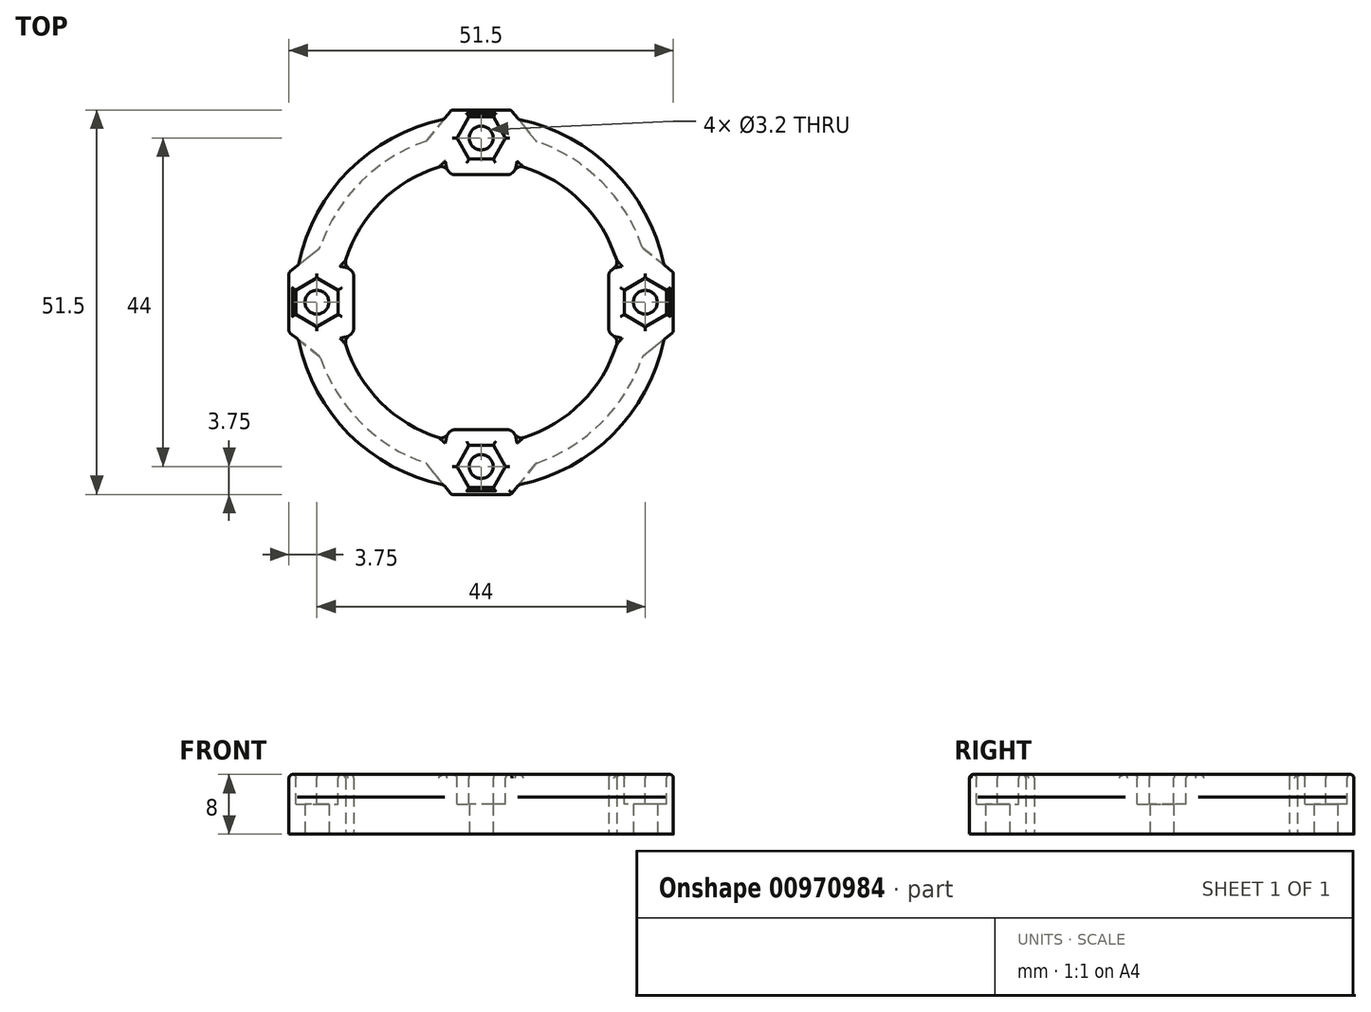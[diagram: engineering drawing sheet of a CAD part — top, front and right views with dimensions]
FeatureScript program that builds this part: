
annotation { "Feature Type Name" : "Feature", "Feature Type Description" : "" }
export const myFeature = defineFeature(function(context is Context, id is Id, definition is map)
    precondition{}
    {
        {
            var Q0;
            Q0=qCreatedBy(makeId("Top.planeOp"),FACE);
            var sketch = newSketch(context, id + "F0", { "sketchPlane" : qUnion([Q0])});
            skArc(sketch, "E0", {"start": v(-5, 24.5) * mm, "mid": v(-17.68, 17.68) * mm, "end": v(-24.5, 5) * mm});
            skLineSegment(sketch, "E1.bottom", {"start": v(-4, 25.75) * mm, "end": v(4, 25.75) * mm});
            skLineSegment(sketch, "E1.top", {"start": v(-4, -25.75) * mm, "end": v(4, -25.75) * mm});
            skLineSegment(sketch, "E1.left", {"start": v(-25.75, 4) * mm, "end": v(-25.75, -4) * mm});
            skLineSegment(sketch, "E1.right", {"start": v(25.75, 4) * mm, "end": v(25.75, -4) * mm});
            skLineSegment(sketch, "E2", {"start": v(-5, 24.5) * mm, "end": v(-4, 25.75) * mm});
            skLineSegment(sketch, "E3", {"start": v(4, 25.75) * mm, "end": v(5, 24.5) * mm});
            skLineSegment(sketch, "E4.1.0", {"start": v(-24.5, -5) * mm, "end": v(-25.75, -4) * mm});
            skLineSegment(sketch, "E4.1.1", {"start": v(-25.75, 4) * mm, "end": v(-24.5, 5) * mm});
            skLineSegment(sketch, "E4.2.0", {"start": v(5, -24.5) * mm, "end": v(4, -25.75) * mm});
            skLineSegment(sketch, "E4.2.1", {"start": v(-4, -25.75) * mm, "end": v(-5, -24.5) * mm});
            skLineSegment(sketch, "E4.3.0", {"start": v(24.5, 5) * mm, "end": v(25.75, 4) * mm});
            skLineSegment(sketch, "E4.3.1", {"start": v(25.75, -4) * mm, "end": v(24.5, -5) * mm});
            skPoint(sketch, "E5.orphan", {"position": v(-25.75, 25.75) * mm});
            skPoint(sketch, "E6.orphan", {"position": v(25.75, 25.75) * mm});
            skArc(sketch, "E7.trimOffspring", {"start": v(24.5, 5) * mm, "mid": v(17.68, 17.68) * mm, "end": v(5, 24.5) * mm});
            skPoint(sketch, "E8.orphan", {"position": v(25.75, -25.75) * mm});
            skArc(sketch, "E9.trimOffspring", {"start": v(5, -24.5) * mm, "mid": v(17.68, -17.68) * mm, "end": v(24.5, -5) * mm});
            skPoint(sketch, "E10.orphan", {"position": v(-25.75, -25.75) * mm});
            skArc(sketch, "E11.trimOffspring", {"start": v(-24.5, -5) * mm, "mid": v(-17.68, -17.68) * mm, "end": v(-5, -24.5) * mm});
            skCircle(sketch, "E12", {"center": v(0, 22) * mm, "radius": 1.6 * mm});
            skCircle(sketch, "E13", {"center": v(-22, 0) * mm, "radius": 1.6 * mm});
            skCircle(sketch, "E14", {"center": v(22, 0) * mm, "radius": 1.6 * mm});
            skCircle(sketch, "E15", {"center": v(0, -22) * mm, "radius": 1.6 * mm});
            skCircle(sketch, "E16", {"center": v(0, 0) * mm, "radius": 22 * mm, "construction": true});
            skArc(sketch, "E17", {"start": v(-5, 18.33) * mm, "mid": v(-13.44, 13.44) * mm, "end": v(-18.33, 5) * mm});
            skLineSegment(sketch, "E18", {"start": v(-5, 18.33) * mm, "end": v(-4, 17.08) * mm});
            skLineSegment(sketch, "E19", {"start": v(-4, 17.08) * mm, "end": v(4, 17.08) * mm});
            skLineSegment(sketch, "E20", {"start": v(4, 17.08) * mm, "end": v(5, 18.33) * mm});
            skLineSegment(sketch, "E21.1.0", {"start": v(-18.33, -5) * mm, "end": v(-17.08, -4) * mm});
            skLineSegment(sketch, "E21.1.1", {"start": v(-17.08, -4) * mm, "end": v(-17.08, 4) * mm});
            skLineSegment(sketch, "E21.1.2", {"start": v(-17.08, 4) * mm, "end": v(-18.33, 5) * mm});
            skLineSegment(sketch, "E21.2.0", {"start": v(5, -18.33) * mm, "end": v(4, -17.08) * mm});
            skLineSegment(sketch, "E21.2.1", {"start": v(4, -17.08) * mm, "end": v(-4, -17.08) * mm});
            skLineSegment(sketch, "E21.2.2", {"start": v(-4, -17.08) * mm, "end": v(-5, -18.33) * mm});
            skLineSegment(sketch, "E21.3.0", {"start": v(18.33, 5) * mm, "end": v(17.08, 4) * mm});
            skLineSegment(sketch, "E21.3.1", {"start": v(17.08, 4) * mm, "end": v(17.08, -4) * mm});
            skLineSegment(sketch, "E21.3.2", {"start": v(17.08, -4) * mm, "end": v(18.33, -5) * mm});
            skArc(sketch, "E22.trimOffspring", {"start": v(18.33, 5) * mm, "mid": v(13.44, 13.44) * mm, "end": v(5, 18.33) * mm});
            skArc(sketch, "E23.trimOffspring", {"start": v(5, -18.33) * mm, "mid": v(13.44, -13.44) * mm, "end": v(18.33, -5) * mm});
            skArc(sketch, "E24.trimOffspring", {"start": v(-18.33, -5) * mm, "mid": v(-13.44, -13.44) * mm, "end": v(-5, -18.33) * mm});
            skSolve(sketch);
        }
        {
            assignVariable(context, id + "F1", {"name" : "nuth", "anyValue" : 4});
        }
        {
            assignVariable(context, id + "F2", {"name" : "bodyt", "anyValue" : 4});
        }
        {
            var Q0;
            Q0=makeQuery(id+"F0.imprint","IMPRINT",FACE,{"disambiguationData":[TD([[makeQuery(id+"F0.imprint","IMPRINT",EDGE,{"derivedFrom":sQuery(id+"F0.wireOp",EDGE,"E0")}),1.0]])]});
            extrude(context, id + "F3", {"entities" : qUnion([Q0]), "depth" : (getVariable(context, 'nuth') + getVariable(context, 'bodyt')) * mm, "offsetDistance" : 25 * mm});
        }
        {
            var Q0;
            Q0=makeQuery(id+"F3.opExtrude","CAP_FACE",FACE,{"disambiguationData":[OSD([sQuery(id+"F0.wireOp",EDGE,"E0"),sQuery(id+"F0.wireOp",EDGE,"E1.bottom"),sQuery(id+"F0.wireOp",EDGE,"E1.top"),sQuery(id+"F0.wireOp",EDGE,"E1.left"),sQuery(id+"F0.wireOp",EDGE,"E1.right"),sQuery(id+"F0.wireOp",EDGE,"E2"),sQuery(id+"F0.wireOp",EDGE,"E3"),sQuery(id+"F0.wireOp",EDGE,"E4.1.0"),sQuery(id+"F0.wireOp",EDGE,"E4.1.1"),sQuery(id+"F0.wireOp",EDGE,"E4.2.0"),sQuery(id+"F0.wireOp",EDGE,"E4.2.1"),sQuery(id+"F0.wireOp",EDGE,"E4.3.0"),sQuery(id+"F0.wireOp",EDGE,"E4.3.1"),sQuery(id+"F0.wireOp",EDGE,"E7.trimOffspring"),sQuery(id+"F0.wireOp",EDGE,"E9.trimOffspring"),sQuery(id+"F0.wireOp",EDGE,"E11.trimOffspring"),sQuery(id+"F0.wireOp",EDGE,"E12"),sQuery(id+"F0.wireOp",EDGE,"E13"),sQuery(id+"F0.wireOp",EDGE,"E14"),sQuery(id+"F0.wireOp",EDGE,"E15")])],"isStart":false});
            var sketch = newSketch(context, id + "F4", { "sketchPlane" : qUnion([Q0])});
            skCircle(sketch, "E25.0", {"center": v(0, 22) * mm, "radius": 1.6 * mm, "construction": true});
            skCircle(sketch, "E26.cCircle", {"center": v(0, 22) * mm, "radius": 2.83 * mm, "construction": true});
            skLineSegment(sketch, "E26.0", {"start": v(1.63, 24.82) * mm, "end": v(3.26, 22) * mm});
            skLineSegment(sketch, "E26.1", {"start": v(3.26, 22) * mm, "end": v(1.63, 19.17) * mm});
            skLineSegment(sketch, "E26.2", {"start": v(1.63, 19.17) * mm, "end": v(-1.63, 19.17) * mm});
            skLineSegment(sketch, "E26.3", {"start": v(-1.63, 19.17) * mm, "end": v(-3.26, 22) * mm});
            skLineSegment(sketch, "E26.4", {"start": v(-3.26, 22) * mm, "end": v(-1.63, 24.82) * mm});
            skLineSegment(sketch, "E26.5", {"start": v(-1.63, 24.82) * mm, "end": v(1.63, 24.82) * mm});
            skPoint(sketch, "E26.0.midPoint", {"position": v(2.45, 23.41) * mm});
            skCircle(sketch, "E27.1.0", {"center": v(-22, 0) * mm, "radius": 1.6 * mm, "construction": true});
            skCircle(sketch, "E27.1.1", {"center": v(-22, 0) * mm, "radius": 2.83 * mm, "construction": true});
            skLineSegment(sketch, "E27.1.2", {"start": v(-19.17, -1.63) * mm, "end": v(-22, -3.26) * mm});
            skPoint(sketch, "E27.1.3", {"position": v(-23.41, 2.45) * mm});
            skLineSegment(sketch, "E27.1.4", {"start": v(-22, -3.26) * mm, "end": v(-24.82, -1.63) * mm});
            skLineSegment(sketch, "E27.1.5", {"start": v(-24.82, 1.63) * mm, "end": v(-22, 3.26) * mm});
            skLineSegment(sketch, "E27.1.6", {"start": v(-22, 3.26) * mm, "end": v(-19.17, 1.63) * mm});
            skLineSegment(sketch, "E27.1.7", {"start": v(-19.17, 1.63) * mm, "end": v(-19.17, -1.63) * mm});
            skLineSegment(sketch, "E27.1.8", {"start": v(-24.82, -1.63) * mm, "end": v(-24.82, 1.63) * mm});
            skCircle(sketch, "E27.2.0", {"center": v(0, -22) * mm, "radius": 1.6 * mm, "construction": true});
            skCircle(sketch, "E27.2.1", {"center": v(0, -22) * mm, "radius": 2.83 * mm, "construction": true});
            skLineSegment(sketch, "E27.2.2", {"start": v(1.63, -19.17) * mm, "end": v(3.26, -22) * mm});
            skPoint(sketch, "E27.2.3", {"position": v(-2.45, -23.41) * mm});
            skLineSegment(sketch, "E27.2.4", {"start": v(3.26, -22) * mm, "end": v(1.63, -24.82) * mm});
            skLineSegment(sketch, "E27.2.5", {"start": v(-1.63, -24.82) * mm, "end": v(-3.26, -22) * mm});
            skLineSegment(sketch, "E27.2.6", {"start": v(-3.26, -22) * mm, "end": v(-1.63, -19.17) * mm});
            skLineSegment(sketch, "E27.2.7", {"start": v(-1.63, -19.17) * mm, "end": v(1.63, -19.17) * mm});
            skLineSegment(sketch, "E27.2.8", {"start": v(1.63, -24.82) * mm, "end": v(-1.63, -24.82) * mm});
            skCircle(sketch, "E27.3.0", {"center": v(22, 0) * mm, "radius": 1.6 * mm, "construction": true});
            skCircle(sketch, "E27.3.1", {"center": v(22, 0) * mm, "radius": 2.83 * mm, "construction": true});
            skLineSegment(sketch, "E27.3.2", {"start": v(19.17, 1.63) * mm, "end": v(22, 3.26) * mm});
            skPoint(sketch, "E27.3.3", {"position": v(23.41, -2.45) * mm});
            skLineSegment(sketch, "E27.3.4", {"start": v(22, 3.26) * mm, "end": v(24.82, 1.63) * mm});
            skLineSegment(sketch, "E27.3.5", {"start": v(24.82, -1.63) * mm, "end": v(22, -3.26) * mm});
            skLineSegment(sketch, "E27.3.6", {"start": v(22, -3.26) * mm, "end": v(19.17, -1.63) * mm});
            skLineSegment(sketch, "E27.3.7", {"start": v(19.17, -1.63) * mm, "end": v(19.17, 1.63) * mm});
            skLineSegment(sketch, "E27.3.8", {"start": v(24.82, 1.63) * mm, "end": v(24.82, -1.63) * mm});
            skPoint(sketch, "E27.center", {"position": v(0, 0) * mm});
            skSolve(sketch);
        }
        {
            var Q0;
            Q0 = qSketchRegion(id + "F4", true);
            extrude(context, id + "F5", {"entities" : qUnion([Q0]), "operationType" : NewBodyOperationType.REMOVE, "oppositeDirection" : true, "depth" : (getVariable(context, 'nuth')) * mm, "offsetDistance" : 25 * mm});
        }
        {
            var Q0;
            Q0=makeQuery(id+"F3.opExtrude","CAP_FACE",FACE,{"disambiguationData":[OSD([sQuery(id+"F0.wireOp",EDGE,"E0"),sQuery(id+"F0.wireOp",EDGE,"E1.bottom"),sQuery(id+"F0.wireOp",EDGE,"E1.top"),sQuery(id+"F0.wireOp",EDGE,"E1.left"),sQuery(id+"F0.wireOp",EDGE,"E1.right"),sQuery(id+"F0.wireOp",EDGE,"E2"),sQuery(id+"F0.wireOp",EDGE,"E3"),sQuery(id+"F0.wireOp",EDGE,"E4.1.0"),sQuery(id+"F0.wireOp",EDGE,"E4.1.1"),sQuery(id+"F0.wireOp",EDGE,"E4.2.0"),sQuery(id+"F0.wireOp",EDGE,"E4.2.1"),sQuery(id+"F0.wireOp",EDGE,"E4.3.0"),sQuery(id+"F0.wireOp",EDGE,"E4.3.1"),sQuery(id+"F0.wireOp",EDGE,"E7.trimOffspring"),sQuery(id+"F0.wireOp",EDGE,"E9.trimOffspring"),sQuery(id+"F0.wireOp",EDGE,"E11.trimOffspring"),sQuery(id+"F0.wireOp",EDGE,"E12"),sQuery(id+"F0.wireOp",EDGE,"E13"),sQuery(id+"F0.wireOp",EDGE,"E14"),sQuery(id+"F0.wireOp",EDGE,"E15"),sQuery(id+"F0.wireOp",EDGE,"E17"),sQuery(id+"F0.wireOp",EDGE,"E18"),sQuery(id+"F0.wireOp",EDGE,"E19"),sQuery(id+"F0.wireOp",EDGE,"E20"),sQuery(id+"F0.wireOp",EDGE,"E21.1.0"),sQuery(id+"F0.wireOp",EDGE,"E21.1.1"),sQuery(id+"F0.wireOp",EDGE,"E21.1.2"),sQuery(id+"F0.wireOp",EDGE,"E21.2.0"),sQuery(id+"F0.wireOp",EDGE,"E21.2.1"),sQuery(id+"F0.wireOp",EDGE,"E21.2.2"),sQuery(id+"F0.wireOp",EDGE,"E21.3.0"),sQuery(id+"F0.wireOp",EDGE,"E21.3.1"),sQuery(id+"F0.wireOp",EDGE,"E21.3.2"),sQuery(id+"F0.wireOp",EDGE,"E22.trimOffspring"),sQuery(id+"F0.wireOp",EDGE,"E23.trimOffspring"),sQuery(id+"F0.wireOp",EDGE,"E24.trimOffspring")])],"isStart":true});
            var sketch = newSketch(context, id + "F6", { "sketchPlane" : qUnion([Q0])});
            skArc(sketch, "E28.0", {"start": v(-24.5, 5) * mm, "mid": v(-17.68, 17.68) * mm, "end": v(-5, 24.5) * mm});
            skArc(sketch, "E29.0", {"start": v(-5, -24.5) * mm, "mid": v(-17.68, -17.68) * mm, "end": v(-24.5, -5) * mm});
            skArc(sketch, "E30.0", {"start": v(5, 24.5) * mm, "mid": v(17.68, 17.68) * mm, "end": v(24.5, 5) * mm});
            skArc(sketch, "E31.0", {"start": v(24.5, -5) * mm, "mid": v(17.68, -17.68) * mm, "end": v(5, -24.5) * mm});
            skPoint(sketch, "E32.0", {"position": v(25.75, 4) * mm});
            skPoint(sketch, "E33.0", {"position": v(25.75, -4) * mm});
            skPoint(sketch, "E34.0", {"position": v(4, 25.75) * mm});
            skPoint(sketch, "E35.0", {"position": v(-4, 25.75) * mm});
            skPoint(sketch, "E36.0", {"position": v(-25.75, 4) * mm});
            skPoint(sketch, "E37.0", {"position": v(-25.75, -4) * mm});
            skPoint(sketch, "E38.0", {"position": v(-4, -25.75) * mm});
            skPoint(sketch, "E39.0", {"position": v(4, -25.75) * mm});
            skLineSegment(sketch, "E40", {"start": v(-25.75, 4) * mm, "end": v(-21.6, 7.3) * mm});
            skLineSegment(sketch, "E41", {"start": v(-25.75, -4) * mm, "end": v(-21.6, -7.3) * mm});
            skLineSegment(sketch, "E42", {"start": v(-4, -25.75) * mm, "end": v(-7.3, -21.6) * mm});
            skLineSegment(sketch, "E43", {"start": v(4, -25.75) * mm, "end": v(7.3, -21.6) * mm});
            skLineSegment(sketch, "E44", {"start": v(25.75, 4) * mm, "end": v(21.6, 7.3) * mm});
            skLineSegment(sketch, "E45", {"start": v(25.75, -4) * mm, "end": v(21.6, -7.3) * mm});
            skLineSegment(sketch, "E46", {"start": v(4, 25.75) * mm, "end": v(7.3, 21.6) * mm});
            skLineSegment(sketch, "E47", {"start": v(-4, 25.75) * mm, "end": v(-7.3, 21.6) * mm});
            skArc(sketch, "E48", {"start": v(-21.6, -7.3) * mm, "mid": v(-16.12, -16.12) * mm, "end": v(-7.3, -21.6) * mm});
            skArc(sketch, "E49.trimOffspring", {"start": v(-7.3, 21.6) * mm, "mid": v(-16.12, 16.12) * mm, "end": v(-21.6, 7.3) * mm});
            skArc(sketch, "E50.trimOffspring", {"start": v(21.6, 7.3) * mm, "mid": v(16.12, 16.12) * mm, "end": v(7.3, 21.6) * mm});
            skArc(sketch, "E51.trimOffspring", {"start": v(7.3, -21.6) * mm, "mid": v(16.12, -16.12) * mm, "end": v(21.6, -7.3) * mm});
            skSolve(sketch);
        }
        {
            var Q0;
            Q0 = qSketchRegion(id + "F6", true);
            extrude(context, id + "F7", {"entities" : qUnion([Q0]), "operationType" : NewBodyOperationType.REMOVE, "oppositeDirection" : true, "depth" : (getVariable(context, 'nuth') + getVariable(context, 'bodyt') - 3) * mm, "offsetDistance" : 25 * mm});
        }
        {
            var Q0;
            Q0=makeQuery(id+"F3.opExtrude","CAP_FACE",FACE,{"disambiguationData":[OSD([sQuery(id+"F0.wireOp",EDGE,"E0"),sQuery(id+"F0.wireOp",EDGE,"E1.bottom"),sQuery(id+"F0.wireOp",EDGE,"E1.top"),sQuery(id+"F0.wireOp",EDGE,"E1.left"),sQuery(id+"F0.wireOp",EDGE,"E1.right"),sQuery(id+"F0.wireOp",EDGE,"E2"),sQuery(id+"F0.wireOp",EDGE,"E3"),sQuery(id+"F0.wireOp",EDGE,"E4.1.0"),sQuery(id+"F0.wireOp",EDGE,"E4.1.1"),sQuery(id+"F0.wireOp",EDGE,"E4.2.0"),sQuery(id+"F0.wireOp",EDGE,"E4.2.1"),sQuery(id+"F0.wireOp",EDGE,"E4.3.0"),sQuery(id+"F0.wireOp",EDGE,"E4.3.1"),sQuery(id+"F0.wireOp",EDGE,"E7.trimOffspring"),sQuery(id+"F0.wireOp",EDGE,"E9.trimOffspring"),sQuery(id+"F0.wireOp",EDGE,"E11.trimOffspring"),sQuery(id+"F0.wireOp",EDGE,"E12"),sQuery(id+"F0.wireOp",EDGE,"E13"),sQuery(id+"F0.wireOp",EDGE,"E14"),sQuery(id+"F0.wireOp",EDGE,"E15"),sQuery(id+"F0.wireOp",EDGE,"E17"),sQuery(id+"F0.wireOp",EDGE,"E18"),sQuery(id+"F0.wireOp",EDGE,"E19"),sQuery(id+"F0.wireOp",EDGE,"E20"),sQuery(id+"F0.wireOp",EDGE,"E21.1.0"),sQuery(id+"F0.wireOp",EDGE,"E21.1.1"),sQuery(id+"F0.wireOp",EDGE,"E21.1.2"),sQuery(id+"F0.wireOp",EDGE,"E21.2.0"),sQuery(id+"F0.wireOp",EDGE,"E21.2.1"),sQuery(id+"F0.wireOp",EDGE,"E21.2.2"),sQuery(id+"F0.wireOp",EDGE,"E21.3.0"),sQuery(id+"F0.wireOp",EDGE,"E21.3.1"),sQuery(id+"F0.wireOp",EDGE,"E21.3.2"),sQuery(id+"F0.wireOp",EDGE,"E22.trimOffspring"),sQuery(id+"F0.wireOp",EDGE,"E23.trimOffspring"),sQuery(id+"F0.wireOp",EDGE,"E24.trimOffspring")])],"isStart":false});
            var Q1;
            Q1=makeQuery(id+"F3.opExtrude","SWEPT_EDGE",EDGE,{"disambiguationData":[OSD([sQuery(id+"F0.wireOp",EDGE,"E4.3.0"),sQuery(id+"F0.wireOp",EDGE,"E7.trimOffspring")])]});
            var Q2;
            Q2=makeQuery(id+"F3.opExtrude","SWEPT_EDGE",EDGE,{"disambiguationData":[OSD([sQuery(id+"F0.wireOp",EDGE,"E1.right"),sQuery(id+"F0.wireOp",EDGE,"E4.3.0")])]});
            var Q3;
            Q3=makeQuery(id+"F3.opExtrude","SWEPT_EDGE",EDGE,{"disambiguationData":[OSD([sQuery(id+"F0.wireOp",EDGE,"E1.right"),sQuery(id+"F0.wireOp",EDGE,"E4.3.1")])]});
            var Q4;
            Q4=makeQuery(id+"F3.opExtrude","SWEPT_EDGE",EDGE,{"disambiguationData":[OSD([sQuery(id+"F0.wireOp",EDGE,"E4.3.1"),sQuery(id+"F0.wireOp",EDGE,"E9.trimOffspring")])]});
            var Q5;
            Q5=makeQuery(id+"F3.opExtrude","SWEPT_EDGE",EDGE,{"disambiguationData":[OSD([sQuery(id+"F0.wireOp",EDGE,"E4.2.0"),sQuery(id+"F0.wireOp",EDGE,"E9.trimOffspring")])]});
            var Q6;
            Q6=makeQuery(id+"F3.opExtrude","SWEPT_EDGE",EDGE,{"disambiguationData":[OSD([sQuery(id+"F0.wireOp",EDGE,"E1.top"),sQuery(id+"F0.wireOp",EDGE,"E4.2.0")])]});
            var Q7;
            Q7=makeQuery(id+"F7.boolean.opBoolean","COPY",EDGE,{"derivedFrom":makeQuery(id+"F7.opExtrude","SWEPT_EDGE",EDGE,{"disambiguationData":[OSD([sQuery(id+"F6.wireOp",EDGE,"E46"),sQuery(id+"F6.wireOp",EDGE,"E50.trimOffspring")])]})});
            var Q8;
            Q8=makeQuery(id+"F7.boolean.opBoolean","COPY",EDGE,{"derivedFrom":makeQuery(id+"F7.opExtrude","SWEPT_EDGE",EDGE,{"disambiguationData":[OSD([sQuery(id+"F6.wireOp",EDGE,"E44"),sQuery(id+"F6.wireOp",EDGE,"E50.trimOffspring")])]})});
            var Q9;
            Q9=makeQuery(id+"F7.boolean.opBoolean","COPY",EDGE,{"derivedFrom":makeQuery(id+"F7.opExtrude","SWEPT_EDGE",EDGE,{"disambiguationData":[OSD([sQuery(id+"F6.wireOp",EDGE,"E45"),sQuery(id+"F6.wireOp",EDGE,"E51.trimOffspring")])]})});
            var Q10;
            Q10=makeQuery(id+"F3.opExtrude","SWEPT_EDGE",EDGE,{"disambiguationData":[OSD([sQuery(id+"F0.wireOp",EDGE,"E1.bottom"),sQuery(id+"F0.wireOp",EDGE,"E3")])]});
            var Q11;
            Q11=makeQuery(id+"F7.boolean.opBoolean","COPY",EDGE,{"derivedFrom":makeQuery(id+"F7.opExtrude","SWEPT_EDGE",EDGE,{"disambiguationData":[OSD([sQuery(id+"F6.wireOp",EDGE,"E43"),sQuery(id+"F6.wireOp",EDGE,"E51.trimOffspring")])]})});
            var Q12;
            Q12=makeQuery(id+"F3.opExtrude","SWEPT_EDGE",EDGE,{"disambiguationData":[OSD([sQuery(id+"F0.wireOp",EDGE,"E1.bottom"),sQuery(id+"F0.wireOp",EDGE,"E2")])]});
            var Q13;
            Q13=makeQuery(id+"F7.boolean.opBoolean","COPY",EDGE,{"derivedFrom":makeQuery(id+"F7.opExtrude","SWEPT_EDGE",EDGE,{"disambiguationData":[OSD([sQuery(id+"F6.wireOp",EDGE,"E42"),sQuery(id+"F6.wireOp",EDGE,"E48")])]})});
            var Q14;
            Q14=makeQuery(id+"F7.boolean.opBoolean","COPY",EDGE,{"derivedFrom":makeQuery(id+"F7.opExtrude","SWEPT_EDGE",EDGE,{"disambiguationData":[OSD([sQuery(id+"F6.wireOp",EDGE,"E41"),sQuery(id+"F6.wireOp",EDGE,"E48")])]})});
            var Q15;
            Q15=makeQuery(id+"F3.opExtrude","SWEPT_EDGE",EDGE,{"disambiguationData":[OSD([sQuery(id+"F0.wireOp",EDGE,"E1.left"),sQuery(id+"F0.wireOp",EDGE,"E4.1.1")])]});
            var Q16;
            Q16=makeQuery(id+"F3.opExtrude","SWEPT_EDGE",EDGE,{"disambiguationData":[OSD([sQuery(id+"F0.wireOp",EDGE,"E1.left"),sQuery(id+"F0.wireOp",EDGE,"E4.1.0")])]});
            var Q17;
            Q17=makeQuery(id+"F7.boolean.opBoolean","COPY",EDGE,{"derivedFrom":makeQuery(id+"F7.opExtrude","SWEPT_EDGE",EDGE,{"disambiguationData":[OSD([sQuery(id+"F6.wireOp",EDGE,"E40"),sQuery(id+"F6.wireOp",EDGE,"E49.trimOffspring")])]})});
            var Q18;
            Q18=makeQuery(id+"F3.opExtrude","SWEPT_EDGE",EDGE,{"disambiguationData":[OSD([sQuery(id+"F0.wireOp",EDGE,"E4.1.0"),sQuery(id+"F0.wireOp",EDGE,"E11.trimOffspring")])]});
            var Q19;
            Q19=makeQuery(id+"F3.opExtrude","SWEPT_EDGE",EDGE,{"disambiguationData":[OSD([sQuery(id+"F0.wireOp",EDGE,"E0"),sQuery(id+"F0.wireOp",EDGE,"E4.1.1")])]});
            var Q20;
            Q20=makeQuery(id+"F3.opExtrude","SWEPT_EDGE",EDGE,{"disambiguationData":[OSD([sQuery(id+"F0.wireOp",EDGE,"E0"),sQuery(id+"F0.wireOp",EDGE,"E2")])]});
            var Q21;
            Q21=makeQuery(id+"F3.opExtrude","SWEPT_EDGE",EDGE,{"disambiguationData":[OSD([sQuery(id+"F0.wireOp",EDGE,"E3"),sQuery(id+"F0.wireOp",EDGE,"E7.trimOffspring")])]});
            var Q22;
            Q22=makeQuery(id+"F3.opExtrude","SWEPT_EDGE",EDGE,{"disambiguationData":[OSD([sQuery(id+"F0.wireOp",EDGE,"E1.top"),sQuery(id+"F0.wireOp",EDGE,"E4.2.1")])]});
            var Q23;
            Q23=makeQuery(id+"F3.opExtrude","SWEPT_EDGE",EDGE,{"disambiguationData":[OSD([sQuery(id+"F0.wireOp",EDGE,"E4.2.1"),sQuery(id+"F0.wireOp",EDGE,"E11.trimOffspring")])]});
            var Q24;
            Q24=makeQuery(id+"F7.boolean.opBoolean","COPY",EDGE,{"derivedFrom":makeQuery(id+"F7.opExtrude","SWEPT_EDGE",EDGE,{"disambiguationData":[OSD([sQuery(id+"F6.wireOp",EDGE,"E47"),sQuery(id+"F6.wireOp",EDGE,"E49.trimOffspring")])]})});
            fillet(context, id + "F8", {"entities" : qUnion([Q0, Q1, Q2, Q3, Q4, Q5, Q6, Q7, Q8, Q9, Q10, Q11, Q12, Q13, Q14, Q15, Q16, Q17, Q18, Q19, Q20, Q21, Q22, Q23, Q24]), "radius" : 0.5 * mm, "tangentPropagation" : true, "allowEdgeOverflow" : false});
        }
        {
            var Q0;
            Q0=makeQuery(id+"F3.opExtrude","SWEPT_EDGE",EDGE,{"disambiguationData":[OSD([sQuery(id+"F0.wireOp",EDGE,"E21.1.1"),sQuery(id+"F0.wireOp",EDGE,"E21.1.2")])]});
            var Q1;
            Q1=makeQuery(id+"F3.opExtrude","SWEPT_EDGE",EDGE,{"disambiguationData":[OSD([sQuery(id+"F0.wireOp",EDGE,"E17"),sQuery(id+"F0.wireOp",EDGE,"E21.1.2")])]});
            var Q2;
            Q2=makeQuery(id+"F3.opExtrude","SWEPT_EDGE",EDGE,{"disambiguationData":[OSD([sQuery(id+"F0.wireOp",EDGE,"E21.1.0"),sQuery(id+"F0.wireOp",EDGE,"E21.1.1")])]});
            var Q3;
            Q3=makeQuery(id+"F3.opExtrude","SWEPT_EDGE",EDGE,{"disambiguationData":[OSD([sQuery(id+"F0.wireOp",EDGE,"E21.1.0"),sQuery(id+"F0.wireOp",EDGE,"E24.trimOffspring")])]});
            var Q4;
            Q4=makeQuery(id+"F3.opExtrude","SWEPT_EDGE",EDGE,{"disambiguationData":[OSD([sQuery(id+"F0.wireOp",EDGE,"E20"),sQuery(id+"F0.wireOp",EDGE,"E22.trimOffspring")])]});
            var Q5;
            Q5=makeQuery(id+"F3.opExtrude","SWEPT_EDGE",EDGE,{"disambiguationData":[OSD([sQuery(id+"F0.wireOp",EDGE,"E19"),sQuery(id+"F0.wireOp",EDGE,"E20")])]});
            var Q6;
            Q6=makeQuery(id+"F3.opExtrude","SWEPT_EDGE",EDGE,{"disambiguationData":[OSD([sQuery(id+"F0.wireOp",EDGE,"E18"),sQuery(id+"F0.wireOp",EDGE,"E19")])]});
            var Q7;
            Q7=makeQuery(id+"F3.opExtrude","SWEPT_EDGE",EDGE,{"disambiguationData":[OSD([sQuery(id+"F0.wireOp",EDGE,"E17"),sQuery(id+"F0.wireOp",EDGE,"E18")])]});
            var Q8;
            Q8=makeQuery(id+"F3.opExtrude","SWEPT_EDGE",EDGE,{"disambiguationData":[OSD([sQuery(id+"F0.wireOp",EDGE,"E21.3.2"),sQuery(id+"F0.wireOp",EDGE,"E23.trimOffspring")])]});
            var Q9;
            Q9=makeQuery(id+"F3.opExtrude","SWEPT_EDGE",EDGE,{"disambiguationData":[OSD([sQuery(id+"F0.wireOp",EDGE,"E21.3.1"),sQuery(id+"F0.wireOp",EDGE,"E21.3.2")])]});
            var Q10;
            Q10=makeQuery(id+"F3.opExtrude","SWEPT_EDGE",EDGE,{"disambiguationData":[OSD([sQuery(id+"F0.wireOp",EDGE,"E21.3.0"),sQuery(id+"F0.wireOp",EDGE,"E21.3.1")])]});
            var Q11;
            Q11=makeQuery(id+"F3.opExtrude","SWEPT_EDGE",EDGE,{"disambiguationData":[OSD([sQuery(id+"F0.wireOp",EDGE,"E21.3.0"),sQuery(id+"F0.wireOp",EDGE,"E22.trimOffspring")])]});
            var Q12;
            Q12=makeQuery(id+"F3.opExtrude","SWEPT_EDGE",EDGE,{"disambiguationData":[OSD([sQuery(id+"F0.wireOp",EDGE,"E21.2.2"),sQuery(id+"F0.wireOp",EDGE,"E24.trimOffspring")])]});
            var Q13;
            Q13=makeQuery(id+"F3.opExtrude","SWEPT_EDGE",EDGE,{"disambiguationData":[OSD([sQuery(id+"F0.wireOp",EDGE,"E21.2.0"),sQuery(id+"F0.wireOp",EDGE,"E21.2.1")])]});
            var Q14;
            Q14=makeQuery(id+"F3.opExtrude","SWEPT_EDGE",EDGE,{"disambiguationData":[OSD([sQuery(id+"F0.wireOp",EDGE,"E21.2.0"),sQuery(id+"F0.wireOp",EDGE,"E23.trimOffspring")])]});
            var Q15;
            Q15=makeQuery(id+"F3.opExtrude","SWEPT_EDGE",EDGE,{"disambiguationData":[OSD([sQuery(id+"F0.wireOp",EDGE,"E21.2.1"),sQuery(id+"F0.wireOp",EDGE,"E21.2.2")])]});
            fillet(context, id + "F9", {"entities" : qUnion([Q0, Q1, Q2, Q3, Q4, Q5, Q6, Q7, Q8, Q9, Q10, Q11, Q12, Q13, Q14, Q15]), "radius" : 1 * mm, "tangentPropagation" : true, "allowEdgeOverflow" : false});
        }
    });
